# Revit family: Haworth_Cultivate_Table_TopOnly
name_source: partatom
category: Furniture Systems
revit_build: Autodesk Revit 2018 (Build: 20170223_1515(x64)
units: mm (PartAtom-declared; Revit-internal decimal feet)

## family parameters
Always vertical = Yes
Cut with Voids When Loaded = No
Part Type = Normal
Room Calculation Point = No
Round Connector Dimension = Use Diameter
Shared = No
Work Plane-Based = No

## types (2) — shared parameters
Actual Depth = 42"
Depth = 42"
Manufacturer = Haworth
Max. Height = 0"
Max. Width = 0"
Min. Height = 0"
Min. Width = 0"
Size = Verify Final Dim. w/ Haworth
Table Edge Finish = Haworth _ Laminate _ Maple H-AE
Table Finish = Haworth _ Laminate _ Maple H-AE
Table Thickness = 2"
URL = www.haworth.com

## per-type parameters (varying)
| type | Actual Height | Actual Width | Width |
| 42d 96w | 42" | 96" | 96" |
| Worksurface | 2" | 120" | 120" |

## geometry (parser evidence)
native form markers: Sweep x2
no freeform markers — native parametric forms only
